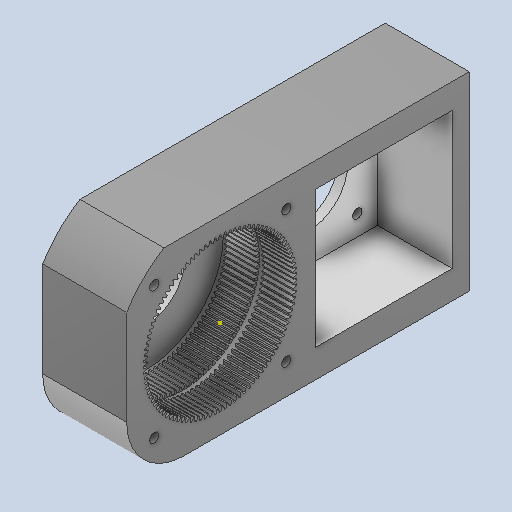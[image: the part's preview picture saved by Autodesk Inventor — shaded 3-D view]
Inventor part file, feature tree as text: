
AUTODESK INVENTOR PART (.ipt)
format: ipt  version: 2022 (Build 260153000, 153)  size: 1,573,376 bytes
history: mixed  units: mm
features: sketch x10, extrude x9, other x3, fillet x1, imported_body x1
ambient origin geometry x8: Origin, YZ Plane, XZ Plane, XY Plane, X Axis, Y Axis, Z Axis, Center Point
bodies: Solid1 (imported_parasolid)
feature tree (24):
  other  "Assembly2.iam"
  other  "96Gears_Stage_1_modified.ipt:1"
  other  "96Gears_Stage_2_modified.ipt:1"
  extrude  "Extrusion6"  TaperAngle=0.0deg  [1 undecoded]
  extrude  "Extrusion7"  Depth=25.0mm
  extrude  "Extrusion8"  Depth=24.0mm TaperAngle=0.0deg
  extrude  "Extrusion9"  Depth=25.0mm
  extrude  "Extrusion10"  Depth=5.5mm
  extrude  "Extrusion11"  Depth=5.2mm
  extrude  "Extrusion12"  Depth=4.0mm
  extrude  "Extrusion13"  Depth=10.0mm
  extrude  "Extrusion14"  Depth=3.0mm TaperAngle=0.0deg
  fillet  "Fillet1"  Radius=18.5mm
  sketch  "Sketch5"  dims[d0=10.0mm d20=0.0mm d21=0.0mm]
  sketch  "Sketch8"  dims[d22=25.0mm d23=0.0mm d24=50.0mm]
  sketch  "Sketch9"  dims[d25=10.0mm d26=0.0mm d32=24.0mm d33=0.0mm]
  sketch  "Sketch10"  dims[d37=3.0mm d38=25.0mm]
  sketch  "Sketch12"  dims[d39=0.0mm d40=0.0mm d41=5.5mm]
  sketch  "Sketch13"  dims[d42=5.2mm d43=5.2mm]
  sketch  "Sketch14"  dims[d44=0.0mm d45=0.0mm d46=4.0mm]
  sketch  "Sketch15"  dims[d47=10.0mm d48=0.0mm d49=25.5mm]
  sketch  "Sketch16"  dims[d50=3.0mm d51=0.0mm d52=3.0mm d53=0.0mm d54=18.5mm]
  sketch  "Sketch17"
  imported_body  NMx_Import_Brep_tag  [imported B-rep: ~803 faces, bbox_mm=[27.0, 61.027756, 110.0]]
note: 1 required parameter value undecoded (feature->parameter linkage not recoverable at this tier; creation-order binding heuristic only, values carry confidence <= 0.55)
